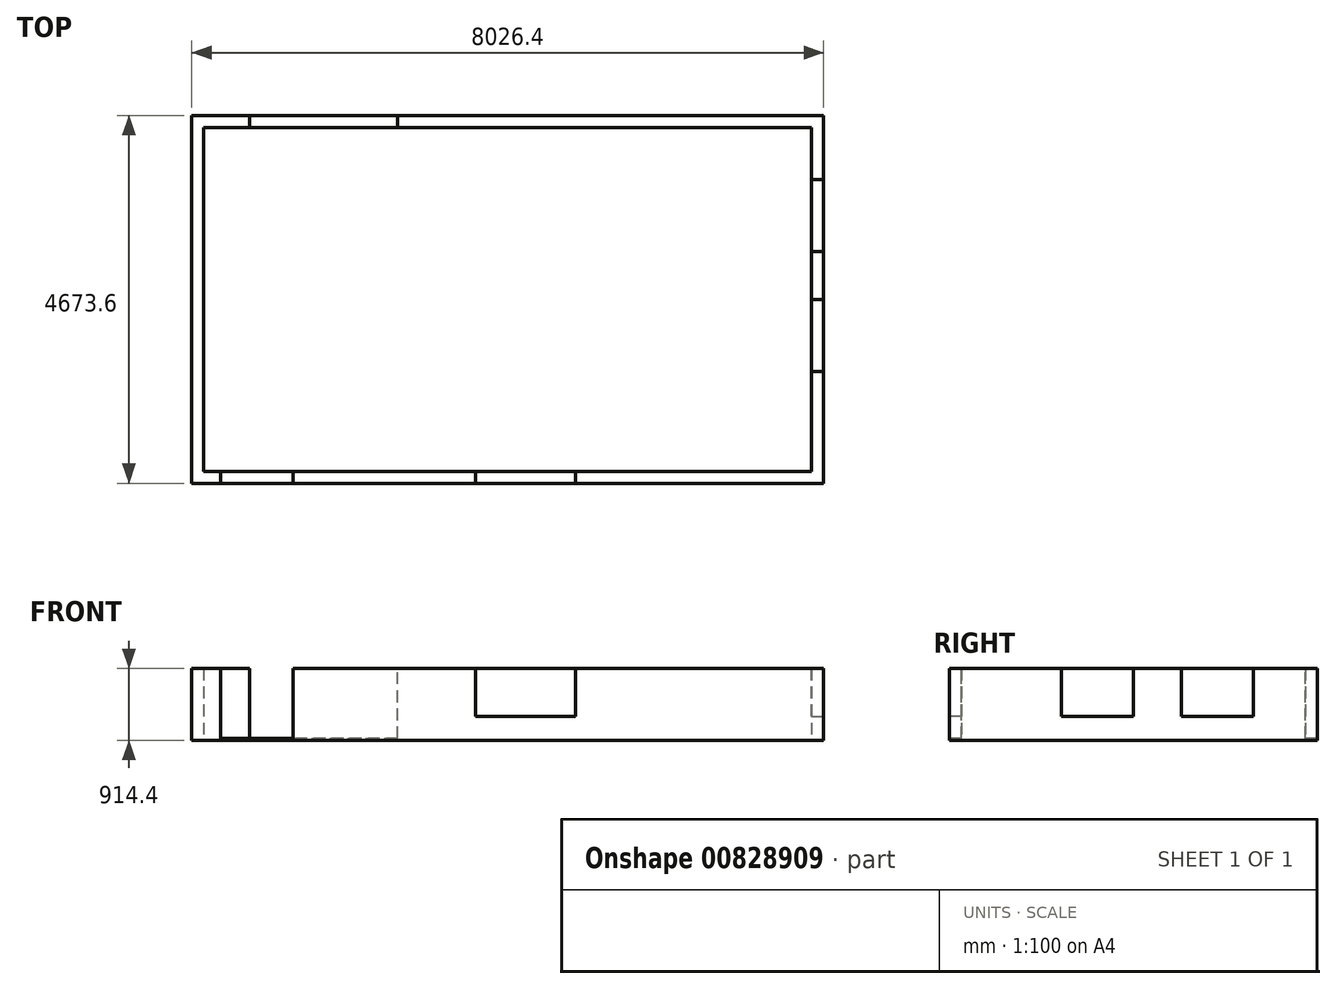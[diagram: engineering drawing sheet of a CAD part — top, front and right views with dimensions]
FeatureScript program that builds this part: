
annotation { "Feature Type Name" : "Feature", "Feature Type Description" : "" }
export const myFeature = defineFeature(function(context is Context, id is Id, definition is map)
    precondition{}
    {
        {
            var Q0;
            Q0=qCreatedBy(makeId("Top.planeOp"),FACE);
            var sketch = newSketch(context, id + "F0", { "sketchPlane" : qUnion([Q0])});
            skLineSegment(sketch, "E0", {"start": v(-2738.44, 1728.84) * mm, "end": v(4983.16, 1728.84) * mm});
            skLineSegment(sketch, "E1", {"start": v(4983.16, 1728.84) * mm, "end": v(4983.16, -2639.96) * mm});
            skLineSegment(sketch, "E2", {"start": v(4983.16, -2639.96) * mm, "end": v(-2738.44, -2639.96) * mm});
            skLineSegment(sketch, "E3", {"start": v(-2738.44, -2639.96) * mm, "end": v(-2738.44, 1728.84) * mm});
            skLineSegment(sketch, "E4", {"start": v(-2890.84, 1881.24) * mm, "end": v(-2890.84, -2792.36) * mm});
            skLineSegment(sketch, "E5", {"start": v(-2890.84, -2792.36) * mm, "end": v(5135.56, -2792.36) * mm});
            skLineSegment(sketch, "E6", {"start": v(5135.56, -2792.36) * mm, "end": v(5135.56, 1881.24) * mm});
            skLineSegment(sketch, "E7", {"start": v(5135.56, 1881.24) * mm, "end": v(-2890.84, 1881.24) * mm});
            skSolve(sketch);
        }
        {
            var Q0;
            Q0 = qSketchRegion(id + "F0", true);
            extrude(context, id + "F1", {"entities" : qUnion([Q0]), "depth" : 914.4 * mm, "offsetDistance" : 25.4 * mm});
        }
        {
            var Q0;
            Q0=makeQuery(id+"F1.opExtrude","CAP_FACE",FACE,{"disambiguationData":[OSD([sQuery(id+"F0.wireOp",EDGE,"E0"),sQuery(id+"F0.wireOp",EDGE,"E1"),sQuery(id+"F0.wireOp",EDGE,"E2"),sQuery(id+"F0.wireOp",EDGE,"E3"),sQuery(id+"F0.wireOp",EDGE,"E4"),sQuery(id+"F0.wireOp",EDGE,"E5"),sQuery(id+"F0.wireOp",EDGE,"E6"),sQuery(id+"F0.wireOp",EDGE,"E7")])],"isStart":false});
            var sketch = newSketch(context, id + "F2", { "sketchPlane" : qUnion([Q0])});
            skLineSegment(sketch, "E8", {"start": v(-2522.54, -2639.96) * mm, "end": v(-2522.54, -2792.36) * mm});
            skLineSegment(sketch, "E9", {"start": v(-2522.54, -2792.36) * mm, "end": v(-1601.8, -2792.36) * mm});
            skLineSegment(sketch, "E10", {"start": v(-1601.8, -2792.36) * mm, "end": v(-1601.8, -2639.96) * mm});
            skLineSegment(sketch, "E11", {"start": v(-1601.8, -2639.96) * mm, "end": v(-2522.54, -2639.96) * mm});
            skLineSegment(sketch, "E12", {"start": v(-2154.24, 1881.24) * mm, "end": v(-2154.24, 1728.84) * mm});
            skLineSegment(sketch, "E13", {"start": v(-2154.24, 1728.84) * mm, "end": v(-274.64, 1728.84) * mm});
            skLineSegment(sketch, "E14", {"start": v(-274.64, 1728.84) * mm, "end": v(-274.64, 1881.24) * mm});
            skLineSegment(sketch, "E15", {"start": v(-274.64, 1881.24) * mm, "end": v(-2154.24, 1881.24) * mm});
            skSolve(sketch);
        }
        {
            var Q0;
            Q0 = qSketchRegion(id + "F2", true);
            extrude(context, id + "F3", {"entities" : qUnion([Q0]), "operationType" : NewBodyOperationType.REMOVE, "oppositeDirection" : true, "depth" : 889 * mm, "offsetDistance" : 25.4 * mm});
        }
        {
            var Q0;
            {var subQ0=sQuery(id+"F0.wireOp",EDGE,"E5");var subQ1=sQuery(id+"F0.wireOp",EDGE,"E2");var subQ2=sQuery(id+"F0.wireOp",EDGE,"E1");var subQ3=sQuery(id+"F0.wireOp",EDGE,"E0");var subQ4=sQuery(id+"F0.wireOp",EDGE,"E6");var subQ5=sQuery(id+"F0.wireOp",EDGE,"E7");Q0=makeQuery(id+"F3.boolean.opBoolean","SPLIT",FACE,{"disambiguationData":[TD([makeQuery(id+"F1.opExtrude","SWEPT_FACE",FACE,{"disambiguationData":[OSD([subQ2])]})])],"derivedFrom":makeQuery(id+"F1.opExtrude","CAP_FACE",FACE,{"disambiguationData":[OSD([subQ3,subQ2,subQ1,sQuery(id+"F0.wireOp",EDGE,"E3"),sQuery(id+"F0.wireOp",EDGE,"E4"),subQ0,subQ4,subQ5])],"isStart":false})});}
            var sketch = newSketch(context, id + "F4", { "sketchPlane" : qUnion([Q0])});
            skLineSegment(sketch, "E16", {"start": v(715.96, -2639.96) * mm, "end": v(715.96, -2792.36) * mm});
            skLineSegment(sketch, "E17", {"start": v(715.96, -2792.36) * mm, "end": v(1985.96, -2792.36) * mm});
            skLineSegment(sketch, "E18", {"start": v(1985.96, -2792.36) * mm, "end": v(1985.96, -2639.96) * mm});
            skLineSegment(sketch, "E19", {"start": v(1985.96, -2639.96) * mm, "end": v(715.96, -2639.96) * mm});
            skLineSegment(sketch, "E20", {"start": v(4983.16, -455.56) * mm, "end": v(4983.16, -1369.96) * mm});
            skLineSegment(sketch, "E21", {"start": v(4983.16, -1369.96) * mm, "end": v(5135.56, -1369.96) * mm});
            skLineSegment(sketch, "E22", {"start": v(5135.56, -1369.96) * mm, "end": v(5135.56, -455.56) * mm});
            skLineSegment(sketch, "E23", {"start": v(5135.56, -455.56) * mm, "end": v(4983.16, -455.56) * mm});
            skLineSegment(sketch, "E24", {"start": v(4983.16, 1068.44) * mm, "end": v(5135.56, 1068.44) * mm});
            skLineSegment(sketch, "E25", {"start": v(5135.56, 1068.44) * mm, "end": v(5135.56, 154.04) * mm});
            skLineSegment(sketch, "E26", {"start": v(5135.56, 154.04) * mm, "end": v(4983.16, 154.04) * mm});
            skLineSegment(sketch, "E27", {"start": v(4983.16, 154.04) * mm, "end": v(4983.16, 1068.44) * mm});
            skSolve(sketch);
        }
        {
            var Q0;
            Q0 = qSketchRegion(id + "F4", true);
            extrude(context, id + "F5", {"entities" : qUnion([Q0]), "operationType" : NewBodyOperationType.REMOVE, "oppositeDirection" : true, "depth" : 609.6 * mm, "offsetDistance" : 25.4 * mm});
        }
    });
